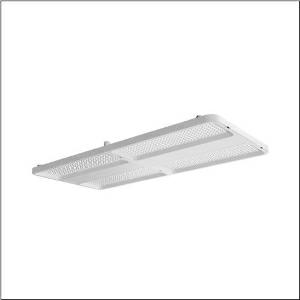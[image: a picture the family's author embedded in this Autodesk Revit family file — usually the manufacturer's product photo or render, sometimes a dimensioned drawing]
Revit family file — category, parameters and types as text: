
# Revit family: highbay_11_maxi_51hn12db4hda
name_source: partatom
category: Lighting Fixtures
units: mm (PartAtom-declared; Revit-internal decimal feet)

## family parameters
Cut with Voids When Loaded = No
Host = Face
Light Source = No
Part Type = Normal
Room Calculation Point = No
Round Connector Dimension = Use Diameter
Shared = No

## types (1)
- --- (1 x LED, 2990 lm, 15.1 W, 4000K)
    Apparent Load = 15 VA
    CIE Flux Codes = 87 98 100 100 100
    Color Rendering = 80
    Color Temperature = 4000K
    Default Elevation = 1800 mm
    Description = high bay luminaire Highbay 11 maxi; direct symmetric wide distribution, light control with lens of PMMA; UGR ≤ 19 (X = 4H | Y = 8H | S = 0.25H | reflection values 70/50/20); luminous flux: 20.000lm; light colour: 840, colour temperature: 4000K, MacAdam ≤ 2 SDCM (initial), colour rendering: CRI > 80; luminous efficacy: 210,7lm/W; rated service life: 100.000h (L95/B50) at AT= 25°C; control: DALI 2; housing frame of high-performance plastic PA6, matt traffic white (RAL 9016); cover of PMMA; dimension (LxWxH): 946 x 442 x 72mm; luminaire connection: terminal, 5-pole, max. 2.5mm² (cable entry for one cable, Ø 8.5..16mm); mains connection: 230..240V, AC/DC 0/50..60Hz; connected load: 94,9W; protection rating (complete): IP66; insulation class (complete): insulation class I (protective earthing); protection symbol: D; impact resistance: IK08; halogen-free wiring; for central battery installations according to DIN EN 60598-2-22; corresponds to IFS (International Featured Standards) requirements for safety and quality in the food industry; LABS conformity tested according to VDMA 24364:2018-05; certification: CE, ENEC, VDE, UKCA; permissible operating ambient temperature: -40..+65°C (reducing of maximum allowable ambient temperature of 5°C with ceiling mounting); packaging unit: 1 piece; (delivery without accessories; please order mounting accessories separately)
    Height = 72 mm  [stored 0.23622 ft]
    Lamp = 1 x LED
    Lamp Light Flux = 2990 lm
    Lamp Power = 15.1 W
    Lamp count = 1
    Length = 946 mm
    Luminous efficacy = 198 lm/W
    Manufacturer = Siteco
    ModVariant = No
    Model = 51HN12DB4HDA
    Mounting Place = Ceiling
    Mounting Type = Pendant
    Number of Poles = 1
    OnlyDefault = Yes
    Power Factor = 1
    Product Name = Highbay 11 maxi
    Product group = high bay luminaire
    ProductGroupID = 901
    Protection Class = Protection class I
    Protection Degree = IP 66
    RLX_Detail_Level = 1
    RLX_Emergency_Light_Flux = 0 lm
    RLX_Emergency_Type = 0
    RLX_Emergency_Type_DB = No
    RlxData = <blob elided: 22201 chars, md5=96eae8ce>
    Socket = socket
    Standby Power = 0 W
    System Light Flux = 2990 lm
    System Power = 15 W
    Type Comments = : DC mode (central or group accumulator) initial emergency light level
    Type Image = l_1363244.jpg
    URL = http://relux.com
    VarID = @adj_005167
    Voltage = 0 V
    Weight = 0.00 kg
    Width = 442 mm

note: [stored X ft] marks values corroborated as IEEE doubles in the binary element streams (Revit-internal decimal feet)

## geometry (parser evidence)
native form markers: Blend x4, Sweep x13
no freeform markers — native parametric forms only
